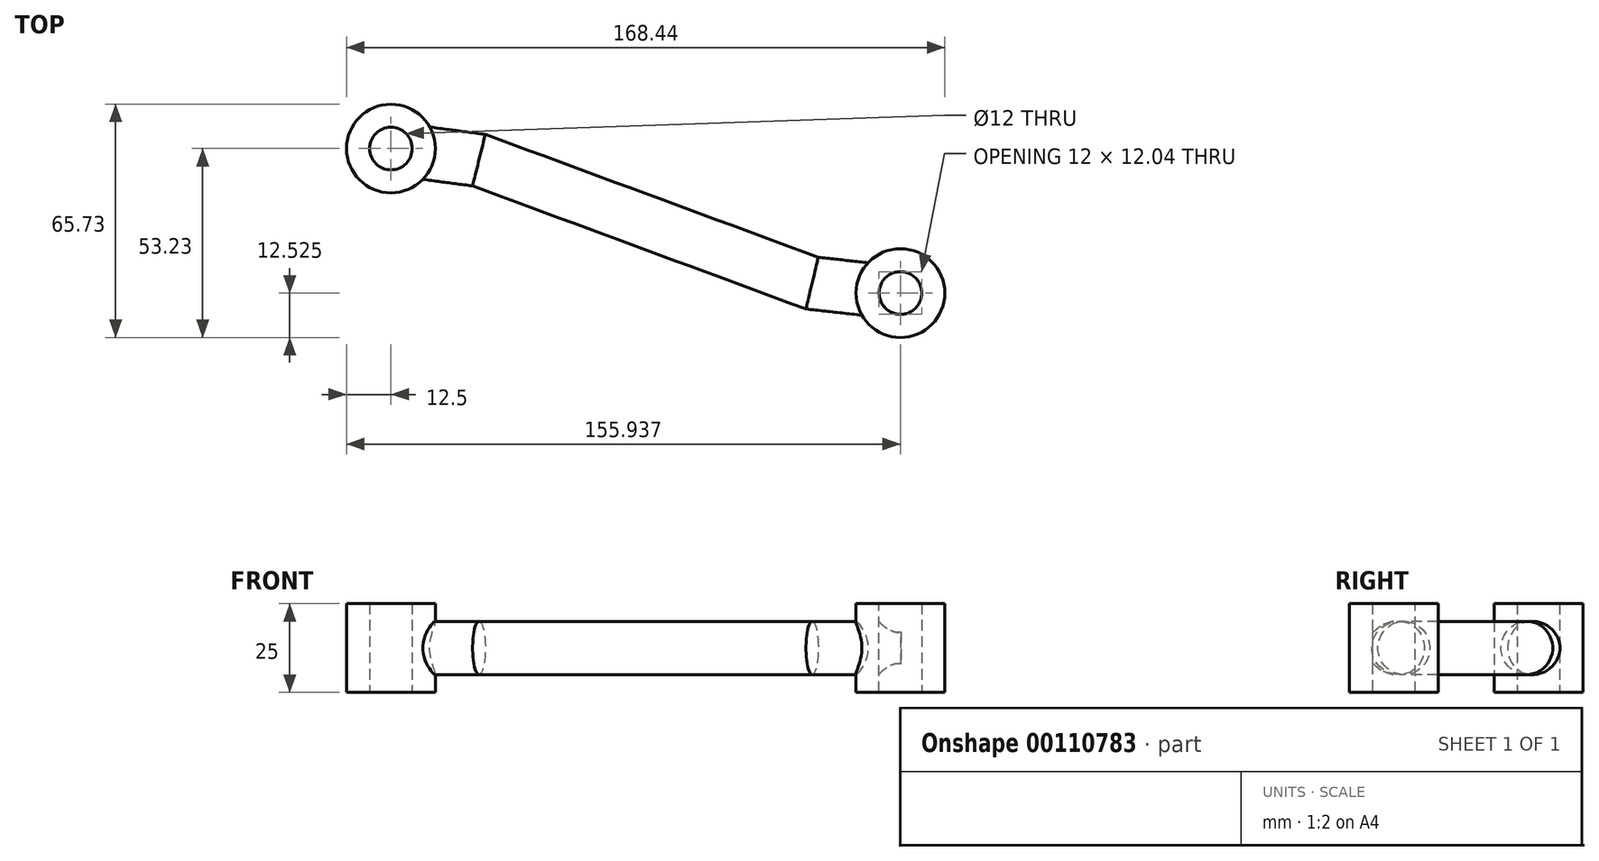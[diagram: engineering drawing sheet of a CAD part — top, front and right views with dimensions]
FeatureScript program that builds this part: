
annotation { "Feature Type Name" : "Feature", "Feature Type Description" : "" }
export const myFeature = defineFeature(function(context is Context, id is Id, definition is map)
    precondition{}
    {
        {
            var Q0;
            Q0=qCreatedBy(makeId("Top.planeOp"),FACE);
            var sketch = newSketch(context, id + "F0", { "sketchPlane" : qUnion([Q0])});
            skLineSegment(sketch, "E0", {"start": v(0, 0) * mm, "end": v(24.79, -3.26) * mm});
            skLineSegment(sketch, "E1", {"start": v(24.79, -3.26) * mm, "end": v(118.59, -37.92) * mm});
            skLineSegment(sketch, "E2", {"start": v(118.59, -37.92) * mm, "end": v(143.44, -40.68) * mm});
            skSolve(sketch);
        }
        {
            var Q0;
            Q0=qCreatedBy(makeId("Right.planeOp"),FACE);
            var sketch = newSketch(context, id + "F1", { "sketchPlane" : qUnion([Q0])});
            skCircle(sketch, "E3", {"center": v(0, 0) * mm, "radius": 7.5 * mm});
            skSolve(sketch);
        }
        {
            var Q0;
            Q0 = qSketchRegion(id + "F1", true);
            var Q1;
            Q1 = qConstructionFilter(qBodyType(qCreatedBy(id + "F0" ,EDGE), BodyType.WIRE), ConstructionObject.NO);
            sweep(context, id + "F2", {"profiles" : qUnion([Q0]), "path" : qUnion([Q1])});
        }
        {
            var Q0;
            Q0=qCreatedBy(makeId("Top.planeOp"),FACE);
            var sketch = newSketch(context, id + "F3", { "sketchPlane" : qUnion([Q0])});
            skCircle(sketch, "E4", {"center": v(0, 0) * mm, "radius": 12.5 * mm});
            skCircle(sketch, "E5", {"center": v(0, 0) * mm, "radius": 6 * mm});
            skCircle(sketch, "E6", {"center": v(143.44, -40.73) * mm, "radius": 12.5 * mm});
            skCircle(sketch, "E7", {"center": v(143.44, -40.73) * mm, "radius": 6 * mm});
            skSolve(sketch);
        }
        {
            var Q0;
            Q0 = qSketchRegion(id + "F3", true);
            extrude(context, id + "F4", {"entities" : qUnion([Q0]), "operationType" : NewBodyOperationType.ADD, "endBound" : BoundingType.SYMMETRIC, "depth" : 25 * mm});
        }
        {
            var Q0;
            Q0=qCreatedBy(makeId("Top.planeOp"),FACE);
            var sketch = newSketch(context, id + "F5", { "sketchPlane" : qUnion([Q0])});
            skCircle(sketch, "E8", {"center": v(0, 0) * mm, "radius": 6 * mm});
            skCircle(sketch, "E9", {"center": v(143.44, -40.68) * mm, "radius": 6 * mm});
            skSolve(sketch);
        }
        {
            var Q0;
            Q0 = qSketchRegion(id + "F5", true);
            extrude(context, id + "F6", {"entities" : qUnion([Q0]), "operationType" : NewBodyOperationType.REMOVE, "endBound" : BoundingType.SYMMETRIC, "oppositeDirection" : true, "depth" : 50 * mm});
        }
    });
